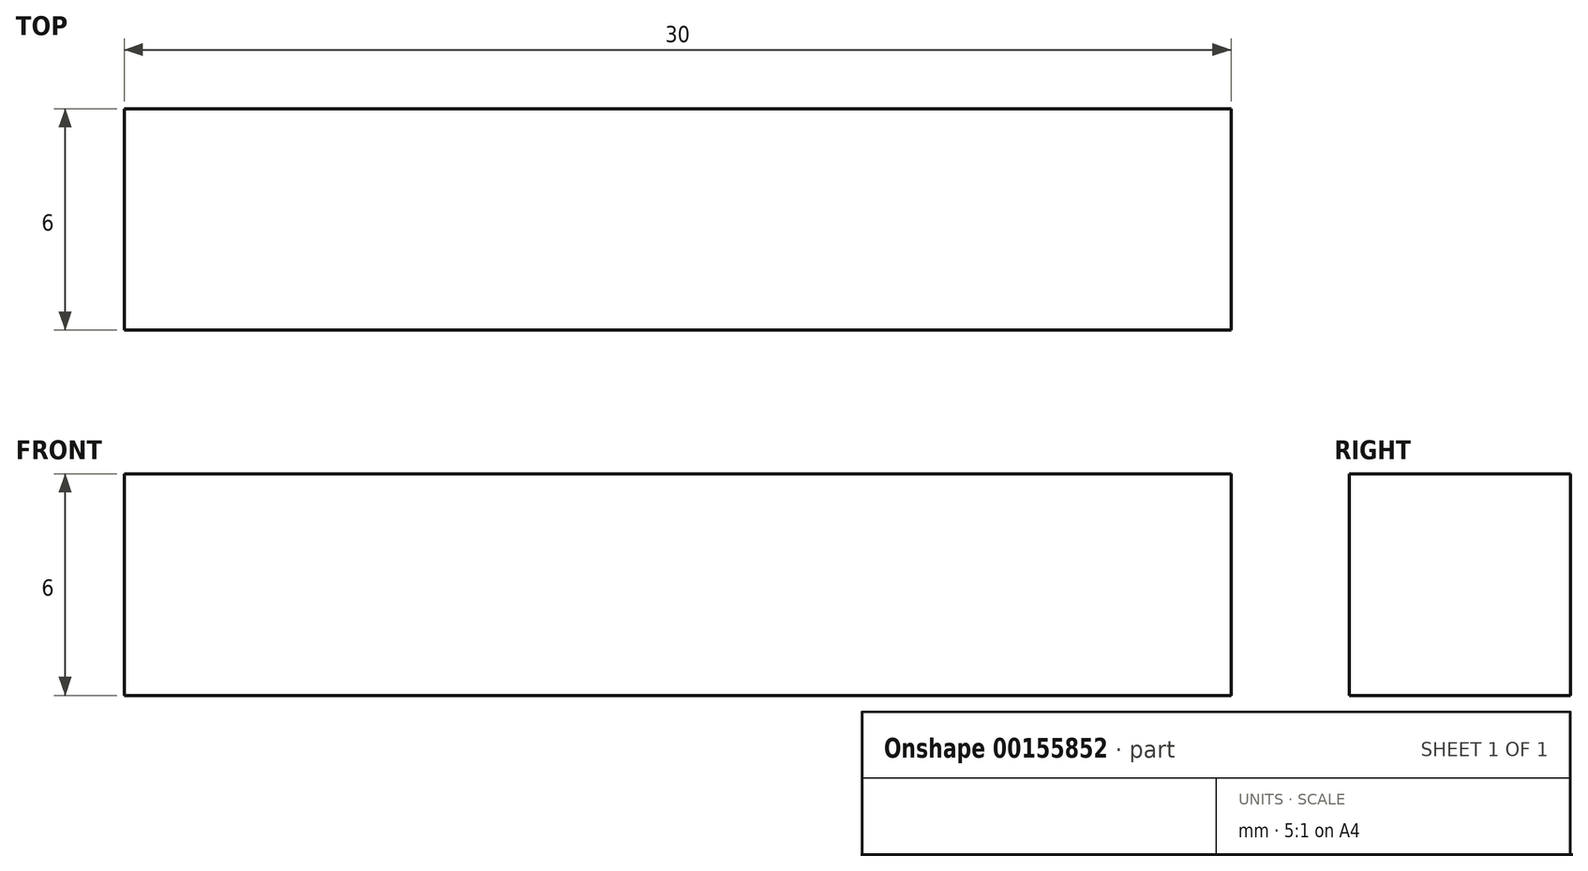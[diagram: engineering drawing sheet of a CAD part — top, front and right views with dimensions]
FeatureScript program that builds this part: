
annotation { "Feature Type Name" : "Feature", "Feature Type Description" : "" }
export const myFeature = defineFeature(function(context is Context, id is Id, definition is map)
    precondition{}
    {
        {
            var Q0;
            Q0=qCreatedBy(makeId("Front.planeOp"),FACE);
            var sketch = newSketch(context, id + "F0", { "sketchPlane" : qUnion([Q0])});
            skLineSegment(sketch, "E0.bottom", {"start": v(0, 0) * mm, "end": v(30, 0) * mm});
            skLineSegment(sketch, "E0.top", {"start": v(0, 6) * mm, "end": v(30, 6) * mm});
            skLineSegment(sketch, "E0.left", {"start": v(0, 0) * mm, "end": v(0, 6) * mm});
            skLineSegment(sketch, "E0.right", {"start": v(30, 0) * mm, "end": v(30, 6) * mm});
            skSolve(sketch);
        }
        {
            var Q0;
            Q0=makeQuery(id+"F0.imprint","IMPRINT",FACE,{"disambiguationData":[TD([[makeQuery(id+"F0.imprint","IMPRINT",EDGE,{"derivedFrom":sQuery(id+"F0.wireOp",EDGE,"E0.bottom")}),1.0]])]});
            extrude(context, id + "F1", {"entities" : qUnion([Q0]), "depth" : 6 * mm});
        }
    });
